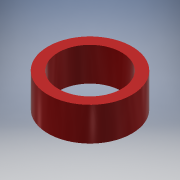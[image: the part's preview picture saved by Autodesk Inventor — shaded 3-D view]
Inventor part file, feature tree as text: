
AUTODESK INVENTOR PART (.ipt)
format: ipt  version: 2019 (Build 230136000, 136)  size: 100,352 bytes
history: native  units: in
note: dims shown in document units (in); Inventor stores cm internally (conversion verified against a paired STEP export)
features: extrude x1, sketch x1
ambient origin geometry x8: Origin, YZ Plane, XZ Plane, XY Plane, X Axis, Y Axis, Z Axis, Center Point
bodies: Solid1 (feature_tree)
feature tree (2):
  extrude  "Extrusion1"  Depth=0.2in
  sketch  "Sketch1"  dims[d0=0.377in d1=0.5in d2=0.2in d3=0.0in]
